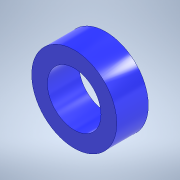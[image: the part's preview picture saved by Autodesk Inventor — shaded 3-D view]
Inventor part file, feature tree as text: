
AUTODESK INVENTOR PART (.ipt)
format: ipt  version: 2022 (Build 260153000, 153)  size: 103,936 bytes
history: native  units: mm
features: extrude x1, sketch x1
ambient origin geometry x8: Origin, YZ Plane, XZ Plane, XY Plane, X Axis, Y Axis, Z Axis, Center Point
bodies: Solid1 (feature_tree)
feature tree (2):
  extrude  "Extrusion1"  Depth=3.0mm
  sketch  "Sketch1"  dims[d0=5.1mm d1=1.5mm d2=3.0mm d3=0.0mm]
